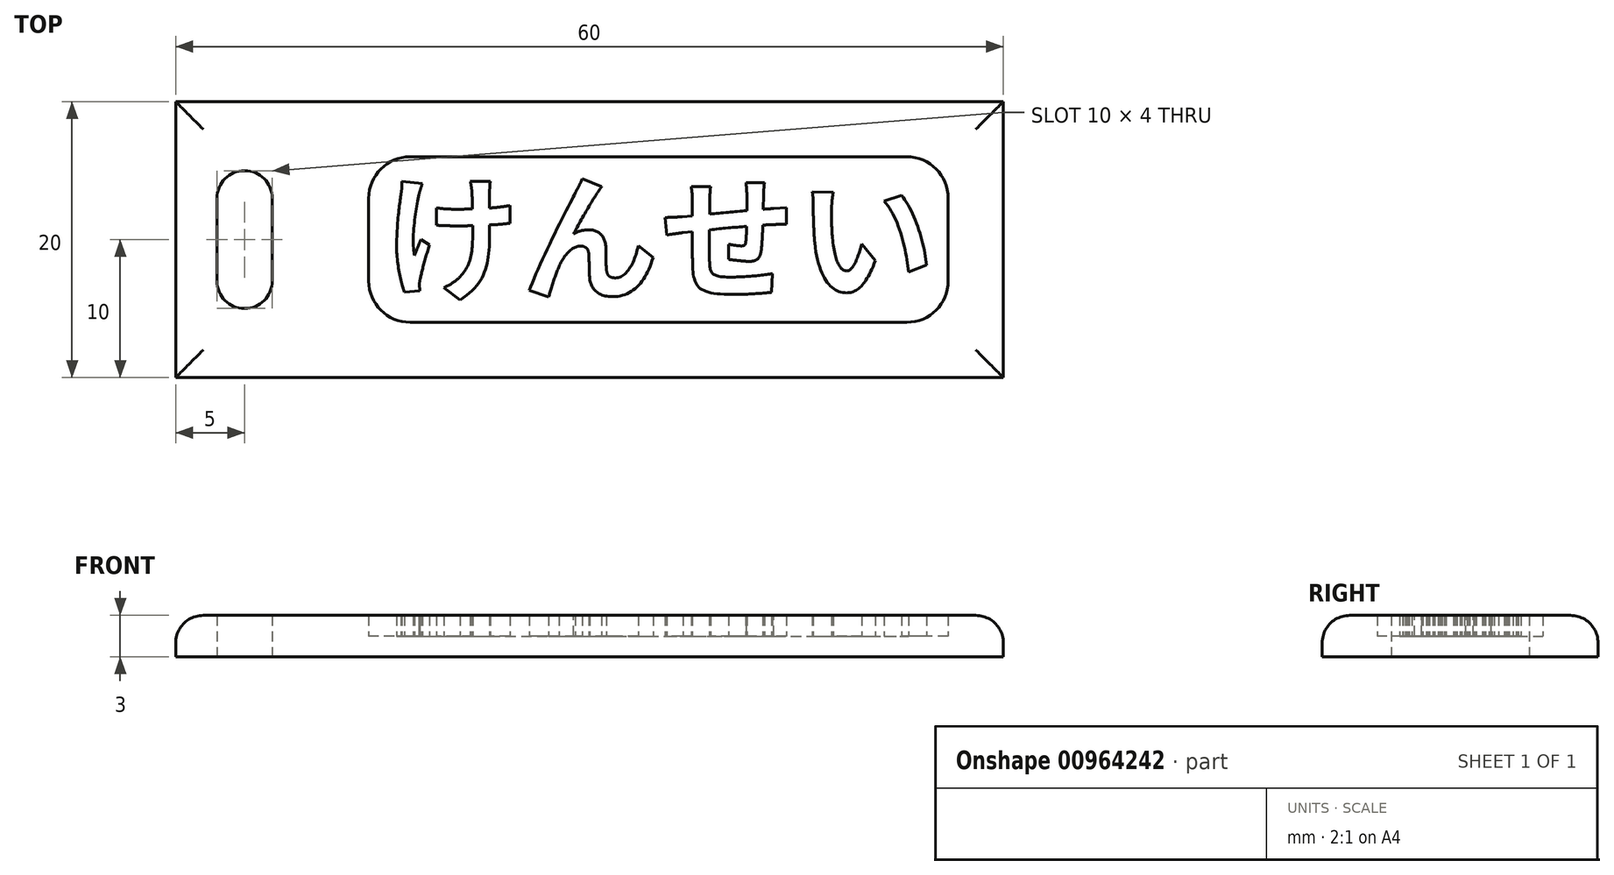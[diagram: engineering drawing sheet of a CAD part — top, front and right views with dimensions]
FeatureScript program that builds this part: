
annotation { "Feature Type Name" : "Feature", "Feature Type Description" : "" }
export const myFeature = defineFeature(function(context is Context, id is Id, definition is map)
    precondition{}
    {
        {
            var Q0;
            Q0=qCreatedBy(makeId("Top.planeOp"),FACE);
            var sketch = newSketch(context, id + "F0", { "sketchPlane" : qUnion([Q0])});
            skLineSegment(sketch, "E0.bottom", {"start": v(-25, 10) * mm, "end": v(25, 10) * mm});
            skLineSegment(sketch, "E0.top", {"start": v(-25, -10) * mm, "end": v(25, -10) * mm});
            skLineSegment(sketch, "E0.left", {"start": v(-25, 10) * mm, "end": v(-25, -10) * mm});
            skLineSegment(sketch, "E0.right", {"start": v(25, 10) * mm, "end": v(25, -10) * mm});
            skPoint(sketch, "E0.middle", {"position": v(0, 0) * mm});
            skLineSegment(sketch, "E1.bottom", {"start": v(-25, 10) * mm, "end": v(-35, 10) * mm});
            skLineSegment(sketch, "E1.top", {"start": v(-25, -10) * mm, "end": v(-35, -10) * mm});
            skLineSegment(sketch, "E1.right", {"start": v(-35, 10) * mm, "end": v(-35, -10) * mm});
            skPoint(sketch, "E1.middle", {"position": v(-30, 0) * mm});
            skPoint(sketch, "E1.middle.positionSnap0", {"position": v(-25, 0) * mm});
            skPoint(sketch, "E1.centerSnap0", {"position": v(-25, 0) * mm});
            skLineSegment(sketch, "E2.bottom", {"start": v(-30, 5) * mm, "end": v(-30, 5) * mm});
            skLineSegment(sketch, "E2.top", {"start": v(-30, -5) * mm, "end": v(-30, -5) * mm});
            skLineSegment(sketch, "E2.left", {"start": v(-32, 3) * mm, "end": v(-32, -3) * mm});
            skLineSegment(sketch, "E2.right", {"start": v(-28, 3) * mm, "end": v(-28, -3) * mm});
            skPoint(sketch, "E3.visualSharp", {"position": v(-32, 5) * mm});
            skArc(sketch, "E3.filletArc", {"start": v(-30, 5) * mm, "mid": v(-31.41, 4.41) * mm, "end": v(-32, 3) * mm});
            skPoint(sketch, "E4.visualSharp", {"position": v(-28, 5) * mm});
            skArc(sketch, "E4.filletArc", {"start": v(-28, 3) * mm, "mid": v(-28.59, 4.41) * mm, "end": v(-30, 5) * mm});
            skPoint(sketch, "E5.visualSharp", {"position": v(-28, -5) * mm});
            skArc(sketch, "E5.filletArc", {"start": v(-30, -5) * mm, "mid": v(-28.59, -4.41) * mm, "end": v(-28, -3) * mm});
            skPoint(sketch, "E6.visualSharp", {"position": v(-32, -5) * mm});
            skArc(sketch, "E6.filletArc", {"start": v(-32, -3) * mm, "mid": v(-31.41, -4.41) * mm, "end": v(-30, -5) * mm});
            skSolve(sketch);
        }
        {
            var Q0;
            Q0=qSketchRegion(id+"F0",true);
            extrude(context, id + "F1", {"entities" : qUnion([Q0]), "depth" : 3 * mm, "offsetDistance" : 25 * mm});
        }
        {
            var Q0;
            Q0=qCreatedBy(makeId("Top.planeOp"),FACE);
            var sketch = newSketch(context, id + "F2", { "sketchPlane" : qUnion([Q0])});
            skLineSegment(sketch, "E7.bottom", {"start": v(-18, 6) * mm, "end": v(18, 6) * mm});
            skLineSegment(sketch, "E7.top", {"start": v(-18, -6) * mm, "end": v(18, -6) * mm});
            skLineSegment(sketch, "E7.left", {"start": v(-21, 3) * mm, "end": v(-21, -3) * mm});
            skLineSegment(sketch, "E7.right", {"start": v(21, 3) * mm, "end": v(21, -3) * mm});
            skPoint(sketch, "E7.middle", {"position": v(0, 0) * mm});
            skPoint(sketch, "E8.visualSharp", {"position": v(-21, 6) * mm});
            skArc(sketch, "E8.filletArc", {"start": v(-18, 6) * mm, "mid": v(-20.12, 5.12) * mm, "end": v(-21, 3) * mm});
            skPoint(sketch, "E9.visualSharp", {"position": v(21, 6) * mm});
            skArc(sketch, "E9.filletArc", {"start": v(21, 3) * mm, "mid": v(20.12, 5.12) * mm, "end": v(18, 6) * mm});
            skPoint(sketch, "E10.visualSharp", {"position": v(21, -6) * mm});
            skArc(sketch, "E10.filletArc", {"start": v(18, -6) * mm, "mid": v(20.12, -5.12) * mm, "end": v(21, -3) * mm});
            skPoint(sketch, "E11.visualSharp", {"position": v(-21, -6) * mm});
            skArc(sketch, "E11.filletArc", {"start": v(-21, -3) * mm, "mid": v(-20.12, -5.12) * mm, "end": v(-18, -6) * mm});
            skSolve(sketch);
        }
        {
            var Q0;
            Q0=qSketchRegion(id+"F2",true);
            extrude(context, id + "F3", {"entities" : qUnion([Q0]), "depth" : 3 * mm, "offsetDistance" : 25 * mm});
        }
        {
            var Q0;
            Q0=makeQuery(id+"F3.opExtrude","SWEPT_BODY",BODY,{"disambiguationData":[OSD([sQuery(id+"F2.wireOp",EDGE,"E7.bottom"),sQuery(id+"F2.wireOp",EDGE,"E7.top"),sQuery(id+"F2.wireOp",EDGE,"E7.left"),sQuery(id+"F2.wireOp",EDGE,"E7.right"),sQuery(id+"F2.wireOp",EDGE,"E8.filletArc"),sQuery(id+"F2.wireOp",EDGE,"E9.filletArc"),sQuery(id+"F2.wireOp",EDGE,"E10.filletArc"),sQuery(id+"F2.wireOp",EDGE,"E11.filletArc")])]});
            transform(context, id + "F4", {"entities" : qUnion([Q0]), "transformType" : TransformType.TRANSLATION_3D, "dx" : 0 * mm, "dy" : 0 * mm, "dz" : 1.5 * mm, "makeCopy" : false});
        }
        {
            var Q0;
            Q0=makeQuery(id+"F3.opExtrude","SWEPT_BODY",BODY,{"disambiguationData":[OSD([sQuery(id+"F2.wireOp",EDGE,"E7.bottom"),sQuery(id+"F2.wireOp",EDGE,"E7.top"),sQuery(id+"F2.wireOp",EDGE,"E7.left"),sQuery(id+"F2.wireOp",EDGE,"E7.right"),sQuery(id+"F2.wireOp",EDGE,"E8.filletArc"),sQuery(id+"F2.wireOp",EDGE,"E9.filletArc"),sQuery(id+"F2.wireOp",EDGE,"E10.filletArc"),sQuery(id+"F2.wireOp",EDGE,"E11.filletArc")])]});
            var Q1;
            Q1=makeQuery(id+"F1.opExtrude","SWEPT_BODY",BODY,{"disambiguationData":[OSD([sQuery(id+"F0.wireOp",EDGE,"E0.bottom"),sQuery(id+"F0.wireOp",EDGE,"E0.top"),sQuery(id+"F0.wireOp",EDGE,"E0.right"),sQuery(id+"F0.wireOp",EDGE,"E1.bottom"),sQuery(id+"F0.wireOp",EDGE,"E1.top"),sQuery(id+"F0.wireOp",EDGE,"E1.right"),sQuery(id+"F0.wireOp",EDGE,"E2.left"),sQuery(id+"F0.wireOp",EDGE,"E2.right"),sQuery(id+"F0.wireOp",EDGE,"E3.filletArc"),sQuery(id+"F0.wireOp",EDGE,"E4.filletArc"),sQuery(id+"F0.wireOp",EDGE,"E5.filletArc"),sQuery(id+"F0.wireOp",EDGE,"E6.filletArc")])]});
            booleanBodies(context, id + "F5", {"operationType" : BooleanOperationType.SUBTRACTION, "tools" : qUnion([Q0]), "targets" : qUnion([Q1])});
        }
        {
            var Q0;
            Q0=qCreatedBy(makeId("Top.planeOp"),FACE);
            var sketch = newSketch(context, id + "F6", { "sketchPlane" : qUnion([Q0])});
            skText(sketch, "E12", { "text": "けんせい", "fontName": "NotoSansCJKjp-Bold.otf"});
            const initialGuessF6  = {"E12": [-0.01995, -0.00369, 1, 0, 0.0072]};
            skSetInitialGuess(sketch, initialGuessF6);
            skSolve(sketch);
        }
        {
            var Q0;
            Q0 = qSketchRegion(id + "F6", true);
            extrude(context, id + "F7", {"entities" : qUnion([Q0]), "operationType" : NewBodyOperationType.ADD, "depth" : 3 * mm, "offsetDistance" : 25 * mm});
        }
        {
            var Q0;
            Q0=makeQuery(id+"F1.opExtrude","CAP_EDGE",EDGE,{"disambiguationData":[OSD([sQuery(id+"F0.wireOp",EDGE,"E0.bottom"),sQuery(id+"F0.wireOp",EDGE,"E1.bottom")])],"isStart":false});
            var Q1;
            Q1=makeQuery(id+"F1.opExtrude","CAP_EDGE",EDGE,{"disambiguationData":[OSD([sQuery(id+"F0.wireOp",EDGE,"E1.right")])],"isStart":false});
            var Q2;
            Q2=makeQuery(id+"F1.opExtrude","CAP_EDGE",EDGE,{"disambiguationData":[OSD([sQuery(id+"F0.wireOp",EDGE,"E0.top"),sQuery(id+"F0.wireOp",EDGE,"E1.top")])],"isStart":false});
            var Q3;
            Q3=makeQuery(id+"F1.opExtrude","CAP_EDGE",EDGE,{"disambiguationData":[OSD([sQuery(id+"F0.wireOp",EDGE,"E0.right")])],"isStart":false});
            fillet(context, id + "F8", {"entities" : qUnion([Q0, Q1, Q2, Q3]), "radius" : 2 * mm, "tangentPropagation" : true, "allowEdgeOverflow" : false});
        }
    });
